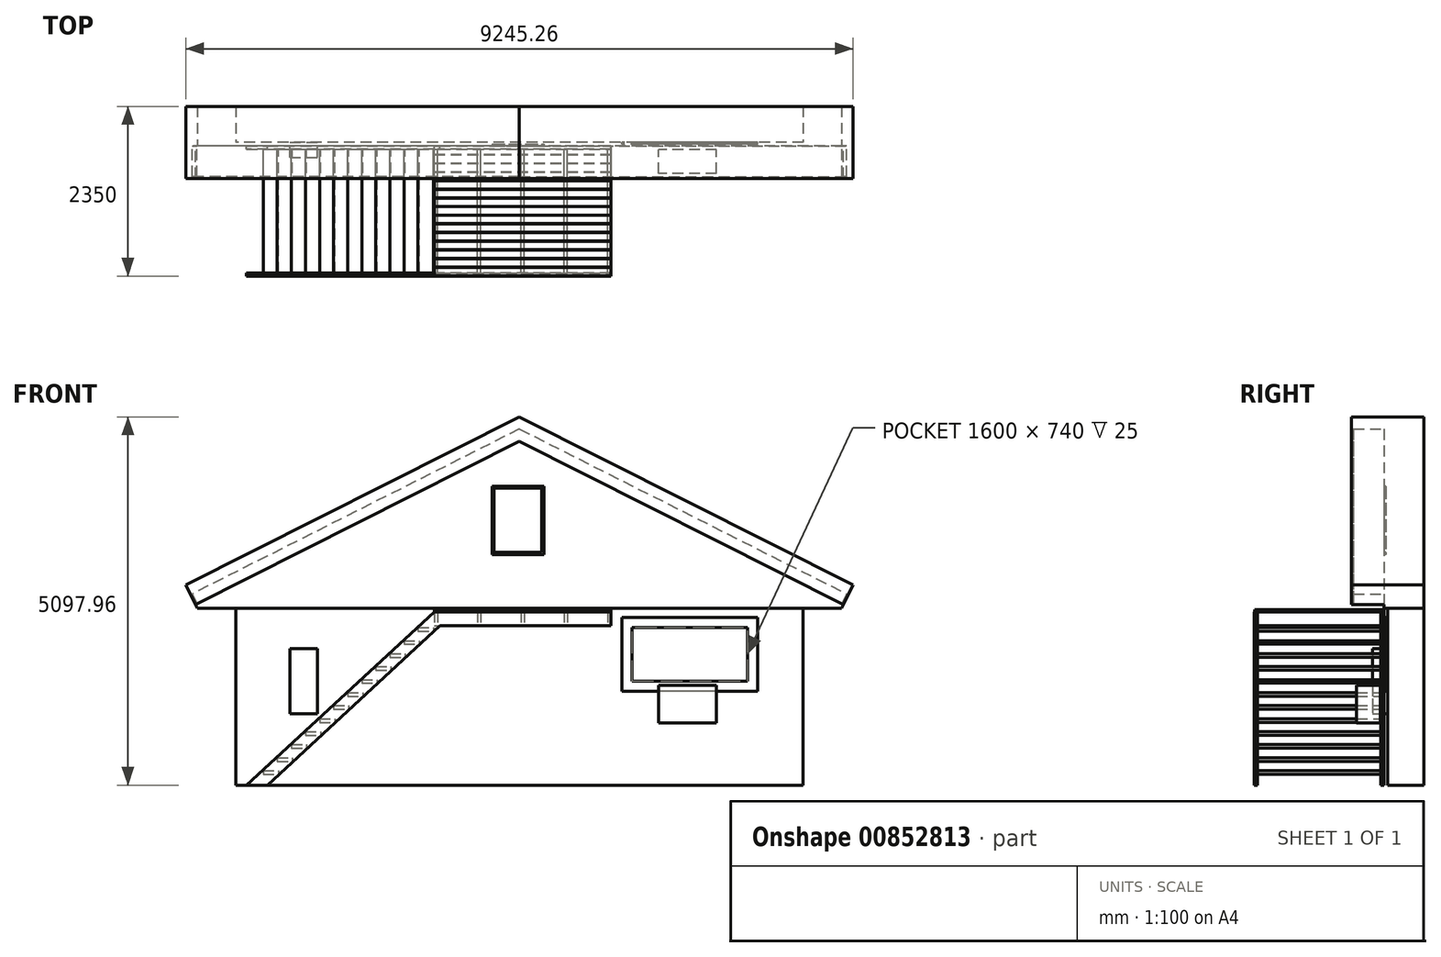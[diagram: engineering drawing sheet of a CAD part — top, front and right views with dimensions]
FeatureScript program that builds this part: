
annotation { "Feature Type Name" : "Feature", "Feature Type Description" : "" }
export const myFeature = defineFeature(function(context is Context, id is Id, definition is map)
    precondition{}
    {
        {
            var Q0;
            Q0=qCreatedBy(makeId("Front.planeOp"),FACE);
            var sketch = newSketch(context, id + "F0", { "sketchPlane" : qUnion([Q0])});
            skLineSegment(sketch, "E0", {"start": v(0, 0) * mm, "end": v(7860, 0) * mm});
            skLineSegment(sketch, "E1", {"start": v(7860, 0) * mm, "end": v(7860, 2950) * mm});
            skLineSegment(sketch, "E2", {"start": v(7860, 2950) * mm, "end": v(3930, 4930) * mm});
            skLineSegment(sketch, "E3", {"start": v(3930, 4930) * mm, "end": v(0, 2950) * mm});
            skLineSegment(sketch, "E4", {"start": v(0, 2950) * mm, "end": v(0, 0) * mm});
            skLineSegment(sketch, "E5", {"start": v(0, 2950) * mm, "end": v(7860, 2950) * mm, "construction": true});
            skLineSegment(sketch, "E6", {"start": v(3930, 2950) * mm, "end": v(3930, 4930) * mm, "construction": true});
            skLineSegment(sketch, "E7.bottom", {"start": v(3550, 4140) * mm, "end": v(4270, 4140) * mm});
            skLineSegment(sketch, "E7.top", {"start": v(3550, 3190) * mm, "end": v(4270, 3190) * mm});
            skLineSegment(sketch, "E7.left", {"start": v(3550, 4140) * mm, "end": v(3550, 3190) * mm});
            skLineSegment(sketch, "E7.right", {"start": v(4270, 4140) * mm, "end": v(4270, 3190) * mm});
            skLineSegment(sketch, "E8", {"start": v(0, 2950) * mm, "end": v(-625.14, 2635.04) * mm});
            skLineSegment(sketch, "E9", {"start": v(-625.14, 2635.04) * mm, "end": v(-692.63, 2769) * mm});
            skLineSegment(sketch, "E10", {"start": v(-692.63, 2769) * mm, "end": v(3930, 5097.96) * mm});
            skLineSegment(sketch, "E11.MirrorCS", {"start": v(8552.63, 2769) * mm, "end": v(3930, 5097.96) * mm});
            skLineSegment(sketch, "E12.MirrorCS", {"start": v(8485.14, 2635.04) * mm, "end": v(8552.63, 2769) * mm});
            skLineSegment(sketch, "E13.MirrorCS", {"start": v(7860, 2950) * mm, "end": v(8485.14, 2635.04) * mm});
            skLineSegment(sketch, "E14.bottom", {"start": v(750, 1890) * mm, "end": v(1130, 1890) * mm});
            skLineSegment(sketch, "E14.top", {"start": v(750, 990) * mm, "end": v(1130, 990) * mm});
            skLineSegment(sketch, "E14.left", {"start": v(750, 1890) * mm, "end": v(750, 990) * mm});
            skLineSegment(sketch, "E14.right", {"start": v(1130, 1890) * mm, "end": v(1130, 990) * mm});
            skLineSegment(sketch, "E15.bottom", {"start": v(5350, 2320) * mm, "end": v(7230, 2320) * mm});
            skLineSegment(sketch, "E15.top", {"start": v(5350, 1300) * mm, "end": v(7230, 1300) * mm});
            skLineSegment(sketch, "E15.left", {"start": v(5350, 2320) * mm, "end": v(5350, 1300) * mm});
            skLineSegment(sketch, "E15.right", {"start": v(7230, 2320) * mm, "end": v(7230, 1300) * mm});
            skLineSegment(sketch, "E16.bottom", {"start": v(5860, 1380) * mm, "end": v(6660, 1380) * mm});
            skLineSegment(sketch, "E16.top", {"start": v(5860, 860) * mm, "end": v(6660, 860) * mm});
            skLineSegment(sketch, "E16.left", {"start": v(5860, 1380) * mm, "end": v(5860, 860) * mm});
            skLineSegment(sketch, "E16.right", {"start": v(6660, 1380) * mm, "end": v(6660, 860) * mm});
            skLineSegment(sketch, "E17", {"start": v(-531.91, 2450) * mm, "end": v(8391.91, 2450) * mm});
            skLineSegment(sketch, "E18", {"start": v(-625.14, 2635.04) * mm, "end": v(-557.65, 2501.08) * mm});
            skLineSegment(sketch, "E19", {"start": v(-557.65, 2501.08) * mm, "end": v(3930, 4762.04) * mm});
            skLineSegment(sketch, "E20.MirrorCS", {"start": v(8417.65, 2501.08) * mm, "end": v(3930, 4762.04) * mm});
            skLineSegment(sketch, "E21.MirrorCS", {"start": v(8485.14, 2635.04) * mm, "end": v(8417.65, 2501.08) * mm});
            skLineSegment(sketch, "E22", {"start": v(8417.65, 2501.08) * mm, "end": v(8391.91, 2450) * mm});
            skLineSegment(sketch, "E23", {"start": v(-557.65, 2501.08) * mm, "end": v(-531.91, 2450) * mm});
            skSolve(sketch);
        }
        {
            var Q0;
            Q0=qCreatedBy(makeId("Front.planeOp"),FACE);
            var sketch = newSketch(context, id + "F1", { "sketchPlane" : qUnion([Q0])});
            skLineSegment(sketch, "E24", {"start": v(0, 0) * mm, "end": v(0, 2450) * mm});
            skLineSegment(sketch, "E25", {"start": v(0, 2450) * mm, "end": v(-531.91, 2450) * mm});
            skLineSegment(sketch, "E26", {"start": v(-531.91, 2450) * mm, "end": v(-692.63, 2769) * mm});
            skLineSegment(sketch, "E27", {"start": v(-692.63, 2769) * mm, "end": v(3930, 5097.96) * mm});
            skLineSegment(sketch, "E28", {"start": v(3930, 5097.96) * mm, "end": v(8552.63, 2769) * mm});
            skLineSegment(sketch, "E29", {"start": v(8552.63, 2769) * mm, "end": v(8391.91, 2450) * mm});
            skLineSegment(sketch, "E30", {"start": v(8391.91, 2450) * mm, "end": v(7860, 2450) * mm});
            skLineSegment(sketch, "E31", {"start": v(7860, 2450) * mm, "end": v(7860, 0) * mm});
            skLineSegment(sketch, "E32", {"start": v(7860, 0) * mm, "end": v(0, 0) * mm});
            skSolve(sketch);
        }
        {
            var Q0;
            Q0 = qSketchRegion(id + "F1", true);
            extrude(context, id + "F2", {"entities" : qUnion([Q0]), "oppositeDirection" : true, "depth" : 500 * mm, "offsetDistance" : 25 * mm});
        }
        {
            var Q0;
            Q0=qCreatedBy(makeId("Front.planeOp"),FACE);
            var sketch = newSketch(context, id + "F3", { "sketchPlane" : qUnion([Q0])});
            skLineSegment(sketch, "E33", {"start": v(-531.91, 2450) * mm, "end": v(-692.63, 2769) * mm});
            skLineSegment(sketch, "E34", {"start": v(-692.63, 2769) * mm, "end": v(3930, 5097.96) * mm});
            skLineSegment(sketch, "E35", {"start": v(3930, 5097.96) * mm, "end": v(8552.63, 2769) * mm});
            skLineSegment(sketch, "E36", {"start": v(8552.63, 2769) * mm, "end": v(8391.91, 2450) * mm});
            skLineSegment(sketch, "E37", {"start": v(8391.91, 2450) * mm, "end": v(-531.91, 2450) * mm});
            skSolve(sketch);
        }
        {
            var Q0;
            Q0 = qSketchRegion(id + "F3", true);
            extrude(context, id + "F4", {"entities" : qUnion([Q0]), "operationType" : NewBodyOperationType.ADD, "depth" : 50 * mm, "offsetDistance" : 25 * mm});
        }
        {
            var Q0;
            Q0=qCreatedBy(makeId("Front.planeOp"),FACE);
            var sketch = newSketch(context, id + "F5", { "sketchPlane" : qUnion([Q0])});
            skLineSegment(sketch, "E38.bottom", {"start": v(7230, 2320) * mm, "end": v(5350, 2320) * mm});
            skLineSegment(sketch, "E38.top", {"start": v(7230, 1300) * mm, "end": v(5350, 1300) * mm});
            skLineSegment(sketch, "E38.left", {"start": v(7230, 2320) * mm, "end": v(7230, 1300) * mm});
            skLineSegment(sketch, "E38.right", {"start": v(5350, 2320) * mm, "end": v(5350, 1300) * mm});
            skLineSegment(sketch, "E39.0", {"start": v(7090, 1440) * mm, "end": v(5490, 1440) * mm});
            skLineSegment(sketch, "E39.1", {"start": v(7090, 2180) * mm, "end": v(7090, 1440) * mm});
            skLineSegment(sketch, "E39.2", {"start": v(7090, 2180) * mm, "end": v(5490, 2180) * mm});
            skLineSegment(sketch, "E39.3", {"start": v(5490, 2180) * mm, "end": v(5490, 1440) * mm});
            skSolve(sketch);
        }
        {
            var Q0;
            Q0 = qSketchRegion(id + "F5", true);
            extrude(context, id + "F6", {"entities" : qUnion([Q0]), "operationType" : NewBodyOperationType.ADD, "depth" : 25 * mm, "offsetDistance" : 25 * mm});
        }
        {
            var Q0;
            Q0=makeQuery(id+"F4.opExtrude","CAP_FACE",FACE,{"disambiguationData":[OSD([sQuery(id+"F3.wireOp",EDGE,"E33"),sQuery(id+"F3.wireOp",EDGE,"E34"),sQuery(id+"F3.wireOp",EDGE,"E35"),sQuery(id+"F3.wireOp",EDGE,"E36"),sQuery(id+"F3.wireOp",EDGE,"E37")])],"isStart":false});
            var sketch = newSketch(context, id + "F7", { "sketchPlane" : qUnion([Q0])});
            skLineSegment(sketch, "E40.0", {"start": v(0, 2950) * mm, "end": v(-602.82, 2646.3) * mm});
            skLineSegment(sketch, "E41.0", {"start": v(3930, 4930) * mm, "end": v(0, 2950) * mm});
            skLineSegment(sketch, "E42.0", {"start": v(-692.63, 2769) * mm, "end": v(3930, 5097.96) * mm});
            skLineSegment(sketch, "E43.0", {"start": v(-625.14, 2635.04) * mm, "end": v(-692.63, 2769) * mm});
            skLineSegment(sketch, "E44", {"start": v(-602.82, 2646.3) * mm, "end": v(-535.32, 2512.33) * mm});
            skPoint(sketch, "E45.orphan", {"position": v(-625.14, 2635.04) * mm});
            skLineSegment(sketch, "E46.0", {"start": v(-625.14, 2635.04) * mm, "end": v(-557.65, 2501.08) * mm});
            skLineSegment(sketch, "E47.MirrorCS", {"start": v(3930, 4930) * mm, "end": v(7860, 2950) * mm});
            skLineSegment(sketch, "E48.MirrorCS", {"start": v(8552.63, 2769) * mm, "end": v(3930, 5097.96) * mm});
            skLineSegment(sketch, "E49.MirrorCS", {"start": v(7860, 2950) * mm, "end": v(8462.82, 2646.3) * mm});
            skLineSegment(sketch, "E50.MirrorCS", {"start": v(8462.82, 2646.3) * mm, "end": v(8395.32, 2512.33) * mm});
            skLineSegment(sketch, "E51.MirrorCS", {"start": v(8485.14, 2635.04) * mm, "end": v(8417.65, 2501.08) * mm});
            skLineSegment(sketch, "E52.MirrorCS", {"start": v(8485.14, 2635.04) * mm, "end": v(8552.63, 2769) * mm});
            skLineSegment(sketch, "E53", {"start": v(-535.32, 2512.33) * mm, "end": v(-557.65, 2501.08) * mm});
            skLineSegment(sketch, "E54", {"start": v(8395.32, 2512.33) * mm, "end": v(8417.65, 2501.08) * mm});
            skSolve(sketch);
        }
        {
            var Q0;
            Q0 = qSketchRegion(id + "F7", true);
            extrude(context, id + "F8", {"entities" : qUnion([Q0]), "operationType" : NewBodyOperationType.ADD, "depth" : 425 * mm, "offsetDistance" : 25 * mm});
        }
        {
            var Q0;
            Q0=makeQuery(id+"F8.opExtrude","CAP_FACE",FACE,{"disambiguationData":[OSD([sQuery(id+"F7.wireOp",EDGE,"E40.0"),sQuery(id+"F7.wireOp",EDGE,"E41.0"),sQuery(id+"F7.wireOp",EDGE,"E42.0"),sQuery(id+"F7.wireOp",EDGE,"E43.0"),sQuery(id+"F7.wireOp",EDGE,"E44"),sQuery(id+"F7.wireOp",EDGE,"E46.0"),sQuery(id+"F7.wireOp",EDGE,"E47.MirrorCS"),sQuery(id+"F7.wireOp",EDGE,"E48.MirrorCS"),sQuery(id+"F7.wireOp",EDGE,"E49.MirrorCS"),sQuery(id+"F7.wireOp",EDGE,"E50.MirrorCS"),sQuery(id+"F7.wireOp",EDGE,"E51.MirrorCS"),sQuery(id+"F7.wireOp",EDGE,"E52.MirrorCS"),sQuery(id+"F7.wireOp",EDGE,"E53"),sQuery(id+"F7.wireOp",EDGE,"E54")])],"isStart":false});
            var sketch = newSketch(context, id + "F9", { "sketchPlane" : qUnion([Q0])});
            skLineSegment(sketch, "E55.0", {"start": v(-692.63, 2769) * mm, "end": v(3930, 5097.96) * mm});
            skLineSegment(sketch, "E56.0", {"start": v(-625.14, 2635.04) * mm, "end": v(-692.63, 2769) * mm});
            skLineSegment(sketch, "E57.0", {"start": v(-625.14, 2635.04) * mm, "end": v(-557.65, 2501.08) * mm});
            skLineSegment(sketch, "E58.0", {"start": v(-557.65, 2501.08) * mm, "end": v(3930, 4762.04) * mm});
            skLineSegment(sketch, "E59.0", {"start": v(8552.63, 2769) * mm, "end": v(3930, 5097.96) * mm});
            skLineSegment(sketch, "E60.0", {"start": v(8417.65, 2501.08) * mm, "end": v(3930, 4762.04) * mm});
            skLineSegment(sketch, "E61.0", {"start": v(8485.14, 2635.04) * mm, "end": v(8552.63, 2769) * mm});
            skLineSegment(sketch, "E62.0", {"start": v(8485.14, 2635.04) * mm, "end": v(8417.65, 2501.08) * mm});
            skSolve(sketch);
        }
        {
            var Q0;
            Q0 = qSketchRegion(id + "F9", true);
            extrude(context, id + "F10", {"entities" : qUnion([Q0]), "operationType" : NewBodyOperationType.ADD, "depth" : 25 * mm, "offsetDistance" : 25 * mm});
        }
        {
            var Q0;
            Q0=makeQuery(id+"F0.imprint","IMPRINT",FACE,{"disambiguationData":[TD([[makeQuery(id+"F0.imprint","IMPRINT",EDGE,{"derivedFrom":sQuery(id+"F0.wireOp",EDGE,"E14.bottom")}),-1.0]])]});
            extrude(context, id + "F11", {"entities" : qUnion([Q0]), "operationType" : NewBodyOperationType.ADD, "depth" : 210 * mm, "offsetDistance" : 25 * mm});
        }
        {
            var Q0;
            Q0=qCreatedBy(makeId("Front.planeOp"),FACE);
            var sketch = newSketch(context, id + "F12", { "sketchPlane" : qUnion([Q0])});
            skLineSegment(sketch, "E63.bottom", {"start": v(6660, 1380) * mm, "end": v(5860, 1380) * mm});
            skLineSegment(sketch, "E63.top", {"start": v(6660, 860) * mm, "end": v(5860, 860) * mm});
            skLineSegment(sketch, "E63.left", {"start": v(6660, 1380) * mm, "end": v(6660, 860) * mm});
            skLineSegment(sketch, "E63.right", {"start": v(5860, 1380) * mm, "end": v(5860, 860) * mm});
            skSolve(sketch);
        }
        {
            var Q0;
            Q0 = qSketchRegion(id + "F12", true);
            extrude(context, id + "F13", {"entities" : qUnion([Q0]), "depth" : 430 * mm, "offsetDistance" : 25 * mm, "hasSecondDirection" : true, "secondDirectionOppositeDirection" : false, "secondDirectionDepth" : 100 * mm});
        }
        {
            var Q0;
            Q0=makeQuery(id+"F4.opExtrude","CAP_FACE",FACE,{"disambiguationData":[OSD([sQuery(id+"F3.wireOp",EDGE,"E33"),sQuery(id+"F3.wireOp",EDGE,"E34"),sQuery(id+"F3.wireOp",EDGE,"E35"),sQuery(id+"F3.wireOp",EDGE,"E36"),sQuery(id+"F3.wireOp",EDGE,"E37")])],"isStart":false});
            var sketch = newSketch(context, id + "F14", { "sketchPlane" : qUnion([Q0])});
            skLineSegment(sketch, "E64.0", {"start": v(3550, 4140) * mm, "end": v(4270, 4140) * mm});
            skLineSegment(sketch, "E65.0", {"start": v(3550, 4140) * mm, "end": v(3550, 3190) * mm});
            skLineSegment(sketch, "E66.0", {"start": v(3550, 3190) * mm, "end": v(4270, 3190) * mm});
            skLineSegment(sketch, "E67.0", {"start": v(4270, 4140) * mm, "end": v(4270, 3190) * mm});
            skLineSegment(sketch, "E68.0", {"start": v(3580, 3220) * mm, "end": v(4240, 3220) * mm});
            skLineSegment(sketch, "E68.1", {"start": v(3580, 4110) * mm, "end": v(3580, 3220) * mm});
            skLineSegment(sketch, "E68.2", {"start": v(3580, 4110) * mm, "end": v(4240, 4110) * mm});
            skLineSegment(sketch, "E68.3", {"start": v(4240, 4110) * mm, "end": v(4240, 3220) * mm});
            skSolve(sketch);
        }
        {
            var Q0;
            Q0 = qSketchRegion(id + "F14", true);
            extrude(context, id + "F15", {"entities" : qUnion([Q0]), "operationType" : NewBodyOperationType.REMOVE, "oppositeDirection" : true, "depth" : 25 * mm, "offsetDistance" : 25 * mm});
        }
        {
            var Q0;
            Q0=qCreatedBy(makeId("Front.planeOp"),FACE);
            cPlane(context, id + "F16", {"entities" : qUnion([Q0]), "cplaneType" : CPlaneType.OFFSET, "offset" : 50 * mm, "width" : 150 * mm, "height" : 150 * mm});
        }
        {
            var Q0;
            Q0=qCreatedBy(id+"F16.planeOp",FACE);
            var sketch = newSketch(context, id + "F17", { "sketchPlane" : qUnion([Q0])});
            skLineSegment(sketch, "E69", {"start": v(5195, 2400) * mm, "end": v(2750, 2400) * mm});
            skLineSegment(sketch, "E70", {"start": v(2750, 2400) * mm, "end": v(150, 0) * mm, "construction": true});
            skLineSegment(sketch, "E71", {"start": v(150, 0) * mm, "end": v(437.5, 0) * mm, "construction": true});
            skLineSegment(sketch, "E72", {"start": v(437.5, 0) * mm, "end": v(2826.24, 2205) * mm, "construction": true});
            skLineSegment(sketch, "E73", {"start": v(2826.24, 2205) * mm, "end": v(5195, 2205) * mm});
            skLineSegment(sketch, "E74", {"start": v(5195, 2205) * mm, "end": v(5195, 2400) * mm});
            skLineSegment(sketch, "E75.bottom", {"start": v(5195, 1100) * mm, "end": v(1629.16, 1100) * mm, "construction": true});
            skLineSegment(sketch, "E75.top", {"start": v(5195, 0) * mm, "end": v(1629.16, 0) * mm, "construction": true});
            skLineSegment(sketch, "E75.left", {"start": v(5195, 1100) * mm, "end": v(5195, 0) * mm, "construction": true});
            skLineSegment(sketch, "E75.right", {"start": v(1629.16, 1100) * mm, "end": v(1629.16, 0) * mm, "construction": true});
            skLineSegment(sketch, "E76", {"start": v(2750, 2400) * mm, "end": v(2750, 2205) * mm});
            skLineSegment(sketch, "E77", {"start": v(2750, 2205) * mm, "end": v(2826.24, 2205) * mm});
            skSolve(sketch);
        }
        {
            var Q0;
            Q0 = qSketchRegion(id + "F17", true);
            extrude(context, id + "F18", {"entities" : qUnion([Q0]), "depth" : 45 * mm, "offsetDistance" : 25 * mm});
        }
        {
            var Q0;
            Q0=qCreatedBy(id+"F16.planeOp",FACE);
            cPlane(context, id + "F19", {"entities" : qUnion([Q0]), "cplaneType" : CPlaneType.OFFSET, "offset" : 1800 * mm, "width" : 150 * mm, "height" : 150 * mm});
        }
        {
            var Q0;
            Q0=qCreatedBy(id+"F19.planeOp",FACE);
            var sketch = newSketch(context, id + "F20", { "sketchPlane" : qUnion([Q0])});
            skLineSegment(sketch, "E78.0", {"start": v(5195, 2205) * mm, "end": v(5195, 2400) * mm});
            skLineSegment(sketch, "E79.0", {"start": v(2826.24, 2205) * mm, "end": v(5195, 2205) * mm});
            skLineSegment(sketch, "E80.0", {"start": v(2750, 2205) * mm, "end": v(2826.24, 2205) * mm});
            skLineSegment(sketch, "E81.0", {"start": v(2750, 2400) * mm, "end": v(2750, 2205) * mm});
            skLineSegment(sketch, "E82.0", {"start": v(5195, 2400) * mm, "end": v(2750, 2400) * mm});
            skSolve(sketch);
        }
        {
            var Q0;
            Q0 = qSketchRegion(id + "F20", true);
            extrude(context, id + "F21", {"entities" : qUnion([Q0]), "oppositeDirection" : true, "depth" : 45 * mm, "offsetDistance" : 25 * mm});
        }
        {
            var Q0;
            Q0=makeQuery(id+"F18.opExtrude","CAP_FACE",FACE,{"disambiguationData":[OSD([sQuery(id+"F17.wireOp",EDGE,"E69"),sQuery(id+"F17.wireOp",EDGE,"E73"),sQuery(id+"F17.wireOp",EDGE,"E74"),sQuery(id+"F17.wireOp",EDGE,"AHIJvJSr-BeLM-72HE-RR8y-DdevRLAzBX8e")])],"isStart":false});
            var sketch = newSketch(context, id + "F22", { "sketchPlane" : qUnion([Q0])});
            skLineSegment(sketch, "E83.bottom", {"start": v(3350, 2400) * mm, "end": v(3395, 2400) * mm});
            skLineSegment(sketch, "E83.top", {"start": v(3350, 2205) * mm, "end": v(3395, 2205) * mm});
            skLineSegment(sketch, "E83.left", {"start": v(3350, 2400) * mm, "end": v(3350, 2205) * mm});
            skLineSegment(sketch, "E83.right", {"start": v(3395, 2400) * mm, "end": v(3395, 2205) * mm});
            skLineSegment(sketch, "E84.bottom", {"start": v(3950, 2400) * mm, "end": v(3995, 2400) * mm});
            skLineSegment(sketch, "E84.top", {"start": v(3950, 2205) * mm, "end": v(3995, 2205) * mm});
            skLineSegment(sketch, "E84.left", {"start": v(3950, 2400) * mm, "end": v(3950, 2205) * mm});
            skLineSegment(sketch, "E84.right", {"start": v(3995, 2400) * mm, "end": v(3995, 2205) * mm});
            skLineSegment(sketch, "E85.bottom", {"start": v(4550, 2400) * mm, "end": v(4595, 2400) * mm});
            skLineSegment(sketch, "E85.top", {"start": v(4550, 2205) * mm, "end": v(4595, 2205) * mm});
            skLineSegment(sketch, "E85.left", {"start": v(4550, 2400) * mm, "end": v(4550, 2205) * mm});
            skLineSegment(sketch, "E85.right", {"start": v(4595, 2400) * mm, "end": v(4595, 2205) * mm});
            skLineSegment(sketch, "E86.bottom", {"start": v(2750, 2400) * mm, "end": v(2795, 2400) * mm});
            skLineSegment(sketch, "E86.top", {"start": v(2750, 2205) * mm, "end": v(2795, 2205) * mm});
            skLineSegment(sketch, "E86.left", {"start": v(2750, 2400) * mm, "end": v(2750, 2205) * mm});
            skLineSegment(sketch, "E86.right", {"start": v(2795, 2400) * mm, "end": v(2795, 2205) * mm});
            skLineSegment(sketch, "E87.bottom", {"start": v(5195, 2400) * mm, "end": v(5150, 2400) * mm});
            skLineSegment(sketch, "E87.top", {"start": v(5195, 2205) * mm, "end": v(5150, 2205) * mm});
            skLineSegment(sketch, "E87.left", {"start": v(5195, 2400) * mm, "end": v(5195, 2205) * mm});
            skLineSegment(sketch, "E87.right", {"start": v(5150, 2400) * mm, "end": v(5150, 2205) * mm});
            skSolve(sketch);
        }
        {
            var Q0;
            Q0 = qSketchRegion(id + "F22", true);
            extrude(context, id + "F23", {"entities" : qUnion([Q0]), "endBound" : BoundingType.UP_TO_NEXT, "depth" : 25 * mm, "offsetDistance" : 25 * mm});
        }
        {
            var Q0;
            Q0=qCreatedBy(id+"F16.planeOp",FACE);
            var sketch = newSketch(context, id + "F24", { "sketchPlane" : qUnion([Q0])});
            skLineSegment(sketch, "E88.0", {"start": v(437.5, 0) * mm, "end": v(2826.24, 2205) * mm});
            skLineSegment(sketch, "E89.0", {"start": v(2750, 2400) * mm, "end": v(150, 0) * mm});
            skLineSegment(sketch, "E90.0", {"start": v(150, 0) * mm, "end": v(437.5, 0) * mm});
            skLineSegment(sketch, "E91.0", {"start": v(2750, 2400) * mm, "end": v(2750, 2205) * mm});
            skLineSegment(sketch, "E92.0", {"start": v(2750, 2205) * mm, "end": v(2826.24, 2205) * mm});
            skSolve(sketch);
        }
        {
            var Q0;
            Q0 = qSketchRegion(id + "F24", true);
            extrude(context, id + "F25", {"entities" : qUnion([Q0]), "operationType" : NewBodyOperationType.ADD, "depth" : 45 * mm, "offsetDistance" : 25 * mm});
        }
        {
            var Q0;
            Q0=qCreatedBy(id+"F19.planeOp",FACE);
            cPlane(context, id + "F26", {"entities" : qUnion([Q0]), "cplaneType" : CPlaneType.OFFSET, "offset" : 900 * mm, "oppositeDirection" : true, "width" : 150 * mm, "height" : 150 * mm});
        }
        {
            var Q0;
            Q0=qCreatedBy(id+"F26.planeOp",FACE);
            var sketch = newSketch(context, id + "F27", { "sketchPlane" : qUnion([Q0])});
            skLineSegment(sketch, "E93.0", {"start": v(437.5, 0) * mm, "end": v(2826.24, 2205) * mm});
            skLineSegment(sketch, "E94.0", {"start": v(2750, 2400) * mm, "end": v(150, 0) * mm});
            skLineSegment(sketch, "E95.0", {"start": v(2750, 2205) * mm, "end": v(2826.24, 2205) * mm});
            skLineSegment(sketch, "E96.0", {"start": v(2750, 2400) * mm, "end": v(2750, 2205) * mm});
            skLineSegment(sketch, "E97.0", {"start": v(150, 0) * mm, "end": v(437.5, 0) * mm});
            skSolve(sketch);
        }
        {
            var Q0;
            Q0=qCreatedBy(id+"F19.planeOp",FACE);
            var sketch = newSketch(context, id + "F28", { "sketchPlane" : qUnion([Q0])});
            skLineSegment(sketch, "E98.0", {"start": v(437.5, 0) * mm, "end": v(2826.24, 2205) * mm});
            skLineSegment(sketch, "E99.0", {"start": v(2750, 2400) * mm, "end": v(150, 0) * mm});
            skLineSegment(sketch, "E100.0", {"start": v(150, 0) * mm, "end": v(437.5, 0) * mm});
            skLineSegment(sketch, "E101.0", {"start": v(2750, 2205) * mm, "end": v(2826.24, 2205) * mm});
            skLineSegment(sketch, "E102.0", {"start": v(2750, 2400) * mm, "end": v(2750, 2205) * mm});
            skSolve(sketch);
        }
        {
            var Q0;
            Q0 = qSketchRegion(id + "F28", true);
            extrude(context, id + "F29", {"entities" : qUnion([Q0]), "operationType" : NewBodyOperationType.ADD, "oppositeDirection" : true, "depth" : 45 * mm, "offsetDistance" : 25 * mm});
        }
        {
            var Q0;
            Q0=makeQuery(id+"F25.boolean.opBoolean","MERGE",FACE,{"derivedFrom":[makeQuery(id+"F18.opExtrude","CAP_FACE",FACE,{"disambiguationData":[OSD([sQuery(id+"F17.wireOp",EDGE,"E69"),sQuery(id+"F17.wireOp",EDGE,"E73"),sQuery(id+"F17.wireOp",EDGE,"E74"),sQuery(id+"F17.wireOp",EDGE,"E76"),sQuery(id+"F17.wireOp",EDGE,"E77")])],"isStart":false}),makeQuery(id+"F25.opExtrude","CAP_FACE",FACE,{"disambiguationData":[OSD([sQuery(id+"F24.wireOp",EDGE,"E88.0"),sQuery(id+"F24.wireOp",EDGE,"E89.0"),sQuery(id+"F24.wireOp",EDGE,"E90.0"),sQuery(id+"F24.wireOp",EDGE,"E91.0"),sQuery(id+"F24.wireOp",EDGE,"E92.0")])],"isStart":false})]});
            var sketch = newSketch(context, id + "F30", { "sketchPlane" : qUnion([Q0])});
            skLineSegment(sketch, "E103.bottom", {"start": v(381.4, 200) * mm, "end": v(591.4, 200) * mm});
            skLineSegment(sketch, "E103.top", {"start": v(381.4, 150) * mm, "end": v(591.4, 150) * mm});
            skLineSegment(sketch, "E103.left", {"start": v(381.4, 200) * mm, "end": v(381.4, 150) * mm});
            skLineSegment(sketch, "E103.right", {"start": v(591.4, 200) * mm, "end": v(591.4, 150) * mm});
            skLineSegment(sketch, "E104.1.0.0", {"start": v(576.4, 330) * mm, "end": v(786.4, 330) * mm});
            skLineSegment(sketch, "E104.1.0.1", {"start": v(786.4, 380) * mm, "end": v(786.4, 330) * mm});
            skLineSegment(sketch, "E104.1.0.2", {"start": v(576.4, 380) * mm, "end": v(786.4, 380) * mm});
            skLineSegment(sketch, "E104.1.0.3", {"start": v(576.4, 380) * mm, "end": v(576.4, 330) * mm});
            skLineSegment(sketch, "E104.2.0.0", {"start": v(771.4, 510) * mm, "end": v(981.4, 510) * mm});
            skLineSegment(sketch, "E104.2.0.1", {"start": v(981.4, 560) * mm, "end": v(981.4, 510) * mm});
            skLineSegment(sketch, "E104.2.0.2", {"start": v(771.4, 560) * mm, "end": v(981.4, 560) * mm});
            skLineSegment(sketch, "E104.2.0.3", {"start": v(771.4, 560) * mm, "end": v(771.4, 510) * mm});
            skLineSegment(sketch, "E104.3.0.0", {"start": v(966.4, 690) * mm, "end": v(1176.4, 690) * mm});
            skLineSegment(sketch, "E104.3.0.1", {"start": v(1176.4, 740) * mm, "end": v(1176.4, 690) * mm});
            skLineSegment(sketch, "E104.3.0.2", {"start": v(966.4, 740) * mm, "end": v(1176.4, 740) * mm});
            skLineSegment(sketch, "E104.3.0.3", {"start": v(966.4, 740) * mm, "end": v(966.4, 690) * mm});
            skLineSegment(sketch, "E104.4.0.0", {"start": v(1161.4, 870) * mm, "end": v(1371.4, 870) * mm});
            skLineSegment(sketch, "E104.4.0.1", {"start": v(1371.4, 920) * mm, "end": v(1371.4, 870) * mm});
            skLineSegment(sketch, "E104.4.0.2", {"start": v(1161.4, 920) * mm, "end": v(1371.4, 920) * mm});
            skLineSegment(sketch, "E104.4.0.3", {"start": v(1161.4, 920) * mm, "end": v(1161.4, 870) * mm});
            skLineSegment(sketch, "E104.direction1", {"start": v(381.4, 150) * mm, "end": v(576.4, 330) * mm, "construction": true});
            skLineSegment(sketch, "E105.0.5.0", {"start": v(1356.4, 1050) * mm, "end": v(1566.4, 1050) * mm});
            skLineSegment(sketch, "E105.3.5.0", {"start": v(1566.4, 1100) * mm, "end": v(1566.4, 1050) * mm});
            skLineSegment(sketch, "E105.6.5.0", {"start": v(1356.4, 1100) * mm, "end": v(1566.4, 1100) * mm});
            skLineSegment(sketch, "E105.9.5.0", {"start": v(1356.4, 1100) * mm, "end": v(1356.4, 1050) * mm});
            skLineSegment(sketch, "E105.0.6.0", {"start": v(1551.4, 1230) * mm, "end": v(1761.4, 1230) * mm});
            skLineSegment(sketch, "E105.3.6.0", {"start": v(1761.4, 1280) * mm, "end": v(1761.4, 1230) * mm});
            skLineSegment(sketch, "E105.6.6.0", {"start": v(1551.4, 1280) * mm, "end": v(1761.4, 1280) * mm});
            skLineSegment(sketch, "E105.9.6.0", {"start": v(1551.4, 1280) * mm, "end": v(1551.4, 1230) * mm});
            skLineSegment(sketch, "E105.0.7.0", {"start": v(1746.4, 1410) * mm, "end": v(1956.4, 1410) * mm});
            skLineSegment(sketch, "E105.3.7.0", {"start": v(1956.4, 1460) * mm, "end": v(1956.4, 1410) * mm});
            skLineSegment(sketch, "E105.6.7.0", {"start": v(1746.4, 1460) * mm, "end": v(1956.4, 1460) * mm});
            skLineSegment(sketch, "E105.9.7.0", {"start": v(1746.4, 1460) * mm, "end": v(1746.4, 1410) * mm});
            skLineSegment(sketch, "E105.0.8.0", {"start": v(1941.4, 1590) * mm, "end": v(2151.4, 1590) * mm});
            skLineSegment(sketch, "E105.3.8.0", {"start": v(2151.4, 1640) * mm, "end": v(2151.4, 1590) * mm});
            skLineSegment(sketch, "E105.6.8.0", {"start": v(1941.4, 1640) * mm, "end": v(2151.4, 1640) * mm});
            skLineSegment(sketch, "E105.9.8.0", {"start": v(1941.4, 1640) * mm, "end": v(1941.4, 1590) * mm});
            skLineSegment(sketch, "E106.0.9.0", {"start": v(2136.4, 1770) * mm, "end": v(2346.4, 1770) * mm});
            skLineSegment(sketch, "E106.3.9.0", {"start": v(2346.4, 1820) * mm, "end": v(2346.4, 1770) * mm});
            skLineSegment(sketch, "E106.6.9.0", {"start": v(2136.4, 1820) * mm, "end": v(2346.4, 1820) * mm});
            skLineSegment(sketch, "E106.9.9.0", {"start": v(2136.4, 1820) * mm, "end": v(2136.4, 1770) * mm});
            skLineSegment(sketch, "E107.0.10.0", {"start": v(2331.4, 1950) * mm, "end": v(2541.4, 1950) * mm});
            skLineSegment(sketch, "E107.3.10.0", {"start": v(2541.4, 2000) * mm, "end": v(2541.4, 1950) * mm});
            skLineSegment(sketch, "E107.6.10.0", {"start": v(2331.4, 2000) * mm, "end": v(2541.4, 2000) * mm});
            skLineSegment(sketch, "E107.9.10.0", {"start": v(2331.4, 2000) * mm, "end": v(2331.4, 1950) * mm});
            skLineSegment(sketch, "E107.0.11.0", {"start": v(2526.4, 2130) * mm, "end": v(2736.4, 2130) * mm});
            skLineSegment(sketch, "E107.3.11.0", {"start": v(2736.4, 2180) * mm, "end": v(2736.4, 2130) * mm});
            skLineSegment(sketch, "E107.6.11.0", {"start": v(2526.4, 2180) * mm, "end": v(2736.4, 2180) * mm});
            skLineSegment(sketch, "E107.9.11.0", {"start": v(2526.4, 2180) * mm, "end": v(2526.4, 2130) * mm});
            skSolve(sketch);
        }
        {
            var Q0;
            Q0 = qSketchRegion(id + "F30", true);
            var Q1;
            Q1=makeQuery(id+"F29.boolean.opBoolean","MERGE",FACE,{"derivedFrom":[makeQuery(id+"F21.opExtrude","CAP_FACE",FACE,{"disambiguationData":[OSD([sQuery(id+"F20.wireOp",EDGE,"E78.0"),sQuery(id+"F20.wireOp",EDGE,"E79.0"),sQuery(id+"F20.wireOp",EDGE,"E80.0"),sQuery(id+"F20.wireOp",EDGE,"E81.0"),sQuery(id+"F20.wireOp",EDGE,"E82.0")])],"isStart":false}),makeQuery(id+"F29.opExtrude","CAP_FACE",FACE,{"disambiguationData":[OSD([sQuery(id+"F28.wireOp",EDGE,"E98.0"),sQuery(id+"F28.wireOp",EDGE,"E99.0"),sQuery(id+"F28.wireOp",EDGE,"E100.0"),sQuery(id+"F28.wireOp",EDGE,"E101.0"),sQuery(id+"F28.wireOp",EDGE,"E102.0")])],"isStart":false})]});
            extrude(context, id + "F31", {"entities" : qUnion([Q0]), "endBound" : BoundingType.UP_TO_SURFACE, "depth" : 25 * mm, "endBoundEntityFace" : qUnion([Q1]), "offsetDistance" : 25 * mm});
        }
        {
            var Q0;
            Q0=makeQuery(id+"F18.opExtrude","SWEPT_FACE",FACE,{"disambiguationData":[OSD([sQuery(id+"F17.wireOp",EDGE,"E69")])]});
            var sketch = newSketch(context, id + "F32", { "sketchPlane" : qUnion([Q0])});
            skLineSegment(sketch, "E108.bottom", {"start": v(2750, -50) * mm, "end": v(5195, -50) * mm});
            skLineSegment(sketch, "E108.top", {"start": v(2750, -165) * mm, "end": v(5195, -165) * mm});
            skLineSegment(sketch, "E108.left", {"start": v(2750, -50) * mm, "end": v(2750, -165) * mm});
            skLineSegment(sketch, "E108.right", {"start": v(5195, -50) * mm, "end": v(5195, -165) * mm});
            skLineSegment(sketch, "E109.0.1.0", {"start": v(2750, -170) * mm, "end": v(2750, -285) * mm});
            skLineSegment(sketch, "E109.0.1.1", {"start": v(2750, -285) * mm, "end": v(5195, -285) * mm});
            skLineSegment(sketch, "E109.0.1.2", {"start": v(2750, -170) * mm, "end": v(5195, -170) * mm});
            skLineSegment(sketch, "E109.0.1.3", {"start": v(5195, -170) * mm, "end": v(5195, -285) * mm});
            skLineSegment(sketch, "E109.0.2.0", {"start": v(2750, -290) * mm, "end": v(2750, -405) * mm});
            skLineSegment(sketch, "E109.0.2.1", {"start": v(2750, -405) * mm, "end": v(5195, -405) * mm});
            skLineSegment(sketch, "E109.0.2.2", {"start": v(2750, -290) * mm, "end": v(5195, -290) * mm});
            skLineSegment(sketch, "E109.0.2.3", {"start": v(5195, -290) * mm, "end": v(5195, -405) * mm});
            skLineSegment(sketch, "E109.0.3.0", {"start": v(2750, -410) * mm, "end": v(2750, -525) * mm});
            skLineSegment(sketch, "E109.0.3.1", {"start": v(2750, -525) * mm, "end": v(5195, -525) * mm});
            skLineSegment(sketch, "E109.0.3.2", {"start": v(2750, -410) * mm, "end": v(5195, -410) * mm});
            skLineSegment(sketch, "E109.0.3.3", {"start": v(5195, -410) * mm, "end": v(5195, -525) * mm});
            skLineSegment(sketch, "E109.0.4.0", {"start": v(2750, -530) * mm, "end": v(2750, -645) * mm});
            skLineSegment(sketch, "E109.0.4.1", {"start": v(2750, -645) * mm, "end": v(5195, -645) * mm});
            skLineSegment(sketch, "E109.0.4.2", {"start": v(2750, -530) * mm, "end": v(5195, -530) * mm});
            skLineSegment(sketch, "E109.0.4.3", {"start": v(5195, -530) * mm, "end": v(5195, -645) * mm});
            skLineSegment(sketch, "E109.0.5.0", {"start": v(2750, -650) * mm, "end": v(2750, -765) * mm});
            skLineSegment(sketch, "E109.0.5.1", {"start": v(2750, -765) * mm, "end": v(5195, -765) * mm});
            skLineSegment(sketch, "E109.0.5.2", {"start": v(2750, -650) * mm, "end": v(5195, -650) * mm});
            skLineSegment(sketch, "E109.0.5.3", {"start": v(5195, -650) * mm, "end": v(5195, -765) * mm});
            skLineSegment(sketch, "E109.0.6.0", {"start": v(2750, -770) * mm, "end": v(2750, -885) * mm});
            skLineSegment(sketch, "E109.0.6.1", {"start": v(2750, -885) * mm, "end": v(5195, -885) * mm});
            skLineSegment(sketch, "E109.0.6.2", {"start": v(2750, -770) * mm, "end": v(5195, -770) * mm});
            skLineSegment(sketch, "E109.0.6.3", {"start": v(5195, -770) * mm, "end": v(5195, -885) * mm});
            skLineSegment(sketch, "E109.0.7.0", {"start": v(2750, -890) * mm, "end": v(2750, -1005) * mm});
            skLineSegment(sketch, "E109.0.7.1", {"start": v(2750, -1005) * mm, "end": v(5195, -1005) * mm});
            skLineSegment(sketch, "E109.0.7.2", {"start": v(2750, -890) * mm, "end": v(5195, -890) * mm});
            skLineSegment(sketch, "E109.0.7.3", {"start": v(5195, -890) * mm, "end": v(5195, -1005) * mm});
            skLineSegment(sketch, "E109.0.8.0", {"start": v(2750, -1010) * mm, "end": v(2750, -1125) * mm});
            skLineSegment(sketch, "E109.0.8.1", {"start": v(2750, -1125) * mm, "end": v(5195, -1125) * mm});
            skLineSegment(sketch, "E109.0.8.2", {"start": v(2750, -1010) * mm, "end": v(5195, -1010) * mm});
            skLineSegment(sketch, "E109.0.8.3", {"start": v(5195, -1010) * mm, "end": v(5195, -1125) * mm});
            skLineSegment(sketch, "E109.0.9.0", {"start": v(2750, -1130) * mm, "end": v(2750, -1245) * mm});
            skLineSegment(sketch, "E109.0.9.1", {"start": v(2750, -1245) * mm, "end": v(5195, -1245) * mm});
            skLineSegment(sketch, "E109.0.9.2", {"start": v(2750, -1130) * mm, "end": v(5195, -1130) * mm});
            skLineSegment(sketch, "E109.0.9.3", {"start": v(5195, -1130) * mm, "end": v(5195, -1245) * mm});
            skLineSegment(sketch, "E109.0.10.0", {"start": v(2750, -1250) * mm, "end": v(2750, -1365) * mm});
            skLineSegment(sketch, "E109.0.10.1", {"start": v(2750, -1365) * mm, "end": v(5195, -1365) * mm});
            skLineSegment(sketch, "E109.0.10.2", {"start": v(2750, -1250) * mm, "end": v(5195, -1250) * mm});
            skLineSegment(sketch, "E109.0.10.3", {"start": v(5195, -1250) * mm, "end": v(5195, -1365) * mm});
            skLineSegment(sketch, "E109.0.11.0", {"start": v(2750, -1370) * mm, "end": v(2750, -1485) * mm});
            skLineSegment(sketch, "E109.0.11.1", {"start": v(2750, -1485) * mm, "end": v(5195, -1485) * mm});
            skLineSegment(sketch, "E109.0.11.2", {"start": v(2750, -1370) * mm, "end": v(5195, -1370) * mm});
            skLineSegment(sketch, "E109.0.11.3", {"start": v(5195, -1370) * mm, "end": v(5195, -1485) * mm});
            skLineSegment(sketch, "E109.0.12.0", {"start": v(2750, -1490) * mm, "end": v(2750, -1605) * mm});
            skLineSegment(sketch, "E109.0.12.1", {"start": v(2750, -1605) * mm, "end": v(5195, -1605) * mm});
            skLineSegment(sketch, "E109.0.12.2", {"start": v(2750, -1490) * mm, "end": v(5195, -1490) * mm});
            skLineSegment(sketch, "E109.0.12.3", {"start": v(5195, -1490) * mm, "end": v(5195, -1605) * mm});
            skLineSegment(sketch, "E109.0.13.0", {"start": v(2750, -1610) * mm, "end": v(2750, -1725) * mm});
            skLineSegment(sketch, "E109.0.13.1", {"start": v(2750, -1725) * mm, "end": v(5195, -1725) * mm});
            skLineSegment(sketch, "E109.0.13.2", {"start": v(2750, -1610) * mm, "end": v(5195, -1610) * mm});
            skLineSegment(sketch, "E109.0.13.3", {"start": v(5195, -1610) * mm, "end": v(5195, -1725) * mm});
            skLineSegment(sketch, "E109.0.14.0", {"start": v(2750, -1730) * mm, "end": v(2750, -1845) * mm});
            skLineSegment(sketch, "E109.0.14.1", {"start": v(2750, -1845) * mm, "end": v(5195, -1845) * mm});
            skLineSegment(sketch, "E109.0.14.2", {"start": v(2750, -1730) * mm, "end": v(5195, -1730) * mm});
            skLineSegment(sketch, "E109.0.14.3", {"start": v(5195, -1730) * mm, "end": v(5195, -1845) * mm});
            skLineSegment(sketch, "E109.direction1", {"start": v(2750, -165) * mm, "end": v(2775, -165) * mm, "construction": true});
            skLineSegment(sketch, "E109.direction2", {"start": v(2750, -165) * mm, "end": v(2750, -285) * mm, "construction": true});
            skSolve(sketch);
        }
        {
            var Q0;
            Q0 = qSketchRegion(id + "F32", true);
            extrude(context, id + "F33", {"entities" : qUnion([Q0]), "depth" : 28 * mm, "offsetDistance" : 25 * mm});
        }
    });
